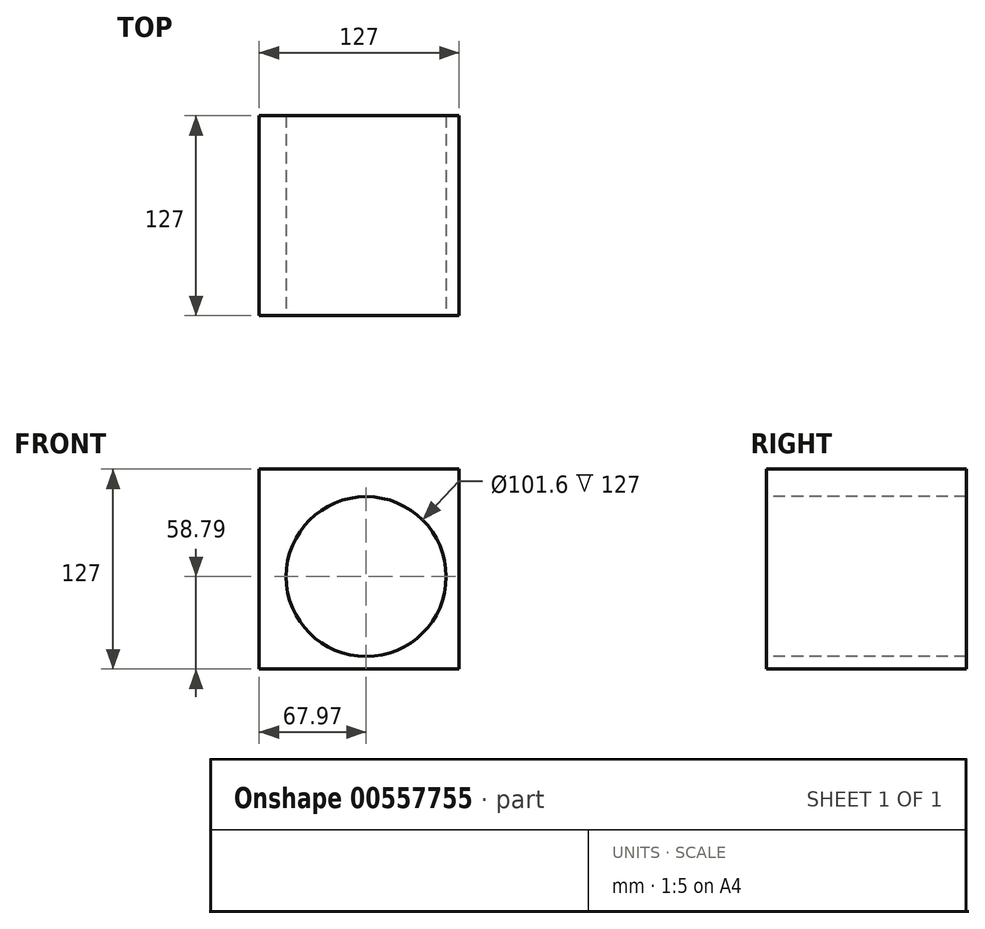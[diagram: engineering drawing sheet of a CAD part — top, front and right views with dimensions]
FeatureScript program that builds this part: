
annotation { "Feature Type Name" : "Feature", "Feature Type Description" : "" }
export const myFeature = defineFeature(function(context is Context, id is Id, definition is map)
    precondition{}
    {
        {
            var Q0;
            Q0=qCreatedBy(makeId("Front.planeOp"),FACE);
            var sketch = newSketch(context, id + "F0", { "sketchPlane" : qUnion([Q0])});
            skLineSegment(sketch, "E0", {"start": v(-67.97, 68.2) * mm, "end": v(59.03, 68.2) * mm});
            skLineSegment(sketch, "E1", {"start": v(59.03, 68.2) * mm, "end": v(59.03, -58.8) * mm});
            skLineSegment(sketch, "E2", {"start": v(59.03, -58.8) * mm, "end": v(-67.97, -58.8) * mm});
            skLineSegment(sketch, "E3", {"start": v(-67.97, -58.8) * mm, "end": v(-67.97, 68.2) * mm});
            skSolve(sketch);
        }
        {
            var Q0;
            Q0 = qSketchRegion(id + "F0", true);
            extrude(context, id + "F1", {"entities" : qUnion([Q0]), "depth" : 127 * mm, "offsetDistance" : 25.4 * mm});
        }
        {
            var Q0;
            Q0=makeQuery(id+"F1.opExtrude","CAP_FACE",FACE,{"disambiguationData":[OSD([sQuery(id+"F0.wireOp",EDGE,"E0"),sQuery(id+"F0.wireOp",EDGE,"E1"),sQuery(id+"F0.wireOp",EDGE,"E2"),sQuery(id+"F0.wireOp",EDGE,"E3")])],"isStart":false});
            var sketch = newSketch(context, id + "F2", { "sketchPlane" : qUnion([Q0])});
            skCircle(sketch, "E4", {"center": v(0, 0) * mm, "radius": 50.8 * mm});
            skSolve(sketch);
        }
        {
            var Q0;
            Q0 = qSketchRegion(id + "F2", true);
            extrude(context, id + "F3", {"entities" : qUnion([Q0]), "operationType" : NewBodyOperationType.REMOVE, "endBound" : BoundingType.THROUGH_ALL, "oppositeDirection" : true, "depth" : 103.89 * mm, "offsetDistance" : 25.4 * mm});
        }
    });
